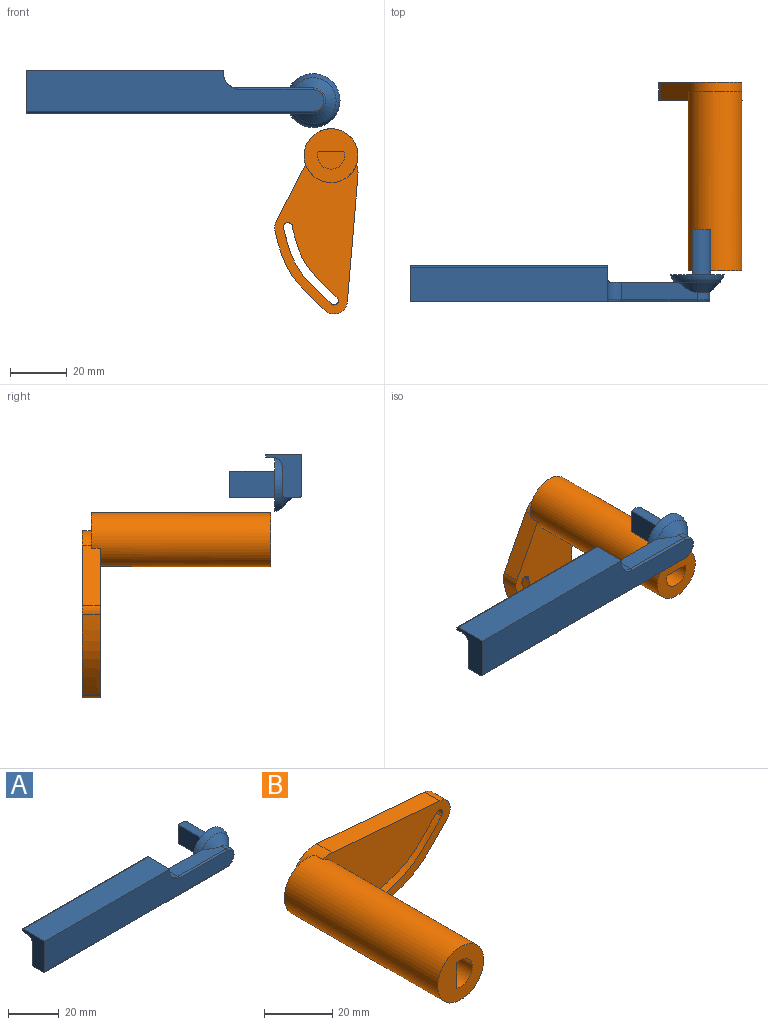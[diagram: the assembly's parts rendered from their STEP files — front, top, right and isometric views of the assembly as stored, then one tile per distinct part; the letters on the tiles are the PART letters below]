
ASSEMBLY  parts=2 mates=1
PART A: 25 faces, bbox 111.1x34.9x23.4 mm
  f0: plane 19.05x19.05mm, normal (0,1,0), area 234.6mm2, adj f3,f22,f23
  f1: plane 26.67x6.22mm, normal (0,0,1), area 150.1mm2, adj f2,f6,f7,f17,f20
  f2: cone r=4.45mm half-angle=45deg, axis (0,1,0), area 152.6mm2, adj f1,f3,f5,f6,f7,f19
  f3: torus R=4.53mm, axis (0,1,0), area 172.6mm2, adj f0,f2
  f4: plane 15.24x12.7mm, normal (-1,0,0), area 113.8mm2, adj f5,f6,f8,f9,f10,f11,f12,f13
  f5: plane 101.6x5.58mm, normal (0,0,-1), area 555.1mm2, adj f2,f4,f7,f15,f19
  f6: plane 94.81x8.26mm, normal (0,1,0), area 774.8mm2, adj f1,f2,f4,f13,f19
  f7: cylinder r=4.45mm len=8.89mm, axis (0,1,0), area 35.5mm2, adj f1,f2,f5,f16
  f8: plane 105.41x14.61mm, normal (0,-1,0), area 1292.5mm2, adj f4,f9,f14,f15,f16,f17,f21
  f9: plane 69.85x12.07mm, normal (0,0,1), area 842.7mm2, adj f4,f8,f14,f18
  f10: plane 69.85x0.64mm, normal (0,1,0), area 44.4mm2, adj f4,f11,f14,f18
  f11: plane 69.85x2.66mm, normal (0,0,-1), area 185.9mm2, adj f4,f10,f12,f14
  f12: cylinder r=3.17mm len=70.94mm, axis (-1,0,0), area 347.7mm2, adj f4,f11,f13,f20
  f13: plane 74.94x1.94mm, normal (0,1,-0.01), area 139.4mm2, adj f4,f6,f12,f20
  f14: plane 12.7x1.31mm, normal (1,0,0), area 16mm2, adj f8,f9,f10,f11,f18,f20,f21
  f15: cylinder r=0.64mm len=101.6mm, axis (1,0,0), area 101.3mm2, adj f4,f5,f8,f16
  f16: torus R=3.81mm, axis (0,-1,0), area 13.2mm2, adj f7,f8,f15,f17
  f17: cylinder r=0.64mm len=26.67mm, axis (-1,0,0), area 26.6mm2, adj f1,f8,f16,f21
  f18: cylinder r=0.64mm len=69.85mm, axis (-1,0,0), area 69.7mm2, adj f4,f9,f10,f14
  f19: cylinder r=0.64mm len=95.58mm, axis (-1,0,0), area 94.8mm2, adj f2,f4,f5,f6
  f20: cylinder r=5.08mm len=9.4mm, axis (0,-1,0), area 51.9mm2, adj f1,f12,f13,f14,f21
  f21: torus R=5.71mm, axis (-1,0,0), area 5.4mm2, adj f8,f14,f17,f20
  f22: plane 15.88x8.98mm, normal (-1,0,0), area 142.6mm2, adj f0,f23,f24
  f23: cylinder r=4.76mm len=15.88mm, axis (0,-1,0), area 288.9mm2, adj f0,f22,f24
  f24: plane 9.53x6.35mm, normal (0,1,0), area 50.5mm2, adj f22,f23
PART B: 20 faces, bbox 65.5x66.7x29.5 mm
  f0: extruded ~10.63x6.35mm, area 71.1mm2, adj f9,f17,f18,f19
  f1: extruded ~26.02x16.6mm, area 200.8mm2, adj f16,f17,f18,f19
  f2: plane 19.05x12.7mm, normal (0,1,0), area 118.7mm2, adj f5,f11,f12
  f3: cylinder r=4.76mm len=25.4mm, axis (0,-1,0), area 462.2mm2, adj f4,f6,f7
  f4: plane 25.4x8.98mm, normal (1,0,0), area 228.1mm2, adj f3,f6,f7
  f5: cylinder r=9.53mm len=63.5mm, axis (0,-1,0), area 3725.5mm2, adj f2,f6,f11,f12,f18
  f6: plane 19.05x19.05mm, normal (0,-1,0), area 234.6mm2, adj f3,f4,f5
  f7: plane 9.53x6.35mm, normal (0,-1,0), area 50.5mm2, adj f3,f4
  f8: extruded ~6.35x1.09mm, area 9.4mm2, adj f9,f16,f17,f18
  f9: extruded ~12.78x11.14mm, area 108.2mm2, adj f0,f8,f17,f18
  f10: cylinder r=4.72mm len=6.35mm, axis (0,-1,0), area 21mm2, adj f11,f15,f17,f18
  f11: plane 21.25x10.97mm, normal (-0.46,0,-0.89), area 148mm2, adj f2,f5,f10,f12,f17,f18
  f12: cylinder r=9.53mm len=17.99mm, axis (0,-1,0), area 95.9mm2, adj f2,f5,f11,f13,f17,f18
  f13: plane 44.55x6.35mm, normal (0.08,0,1), area 283.9mm2, adj f12,f14,f17,f18
  f14: cylinder r=4.72mm len=7.89mm, axis (0,-1,0), area 66.8mm2, adj f13,f15,f17,f18
  f15: extruded ~28.34x17.71mm, area 217.5mm2, adj f10,f14,f17,f18
  f16: cylinder r=1.55mm len=6.35mm, axis (0,-1,0), area 30.9mm2, adj f1,f8,f17,f18
  f17: plane 59.2x29.49mm, normal (0,1,0), area 1108.5mm2, adj f0,f1,f8,f9,f10,f11,f12,f13
  f18: plane 52.96x29.49mm, normal (0,-1,0), area 942.1mm2, adj f0,f1,f5,f8,f9,f10,f11,f12
  f19: cylinder r=1.7mm len=6.35mm, axis (0,1,0), area 43.1mm2, adj f0,f1,f17,f18
PLACE A t=(-53.42,-38.58,3.98)mm
PLACE B rot(axis=(0,1,0),90deg) t=(-47.07,-37.25,-15.52)mm
MATE parallel A.f23 <-> B.f5  axis (0,1,0) through (-53.42,-38.58,3.98)mm
